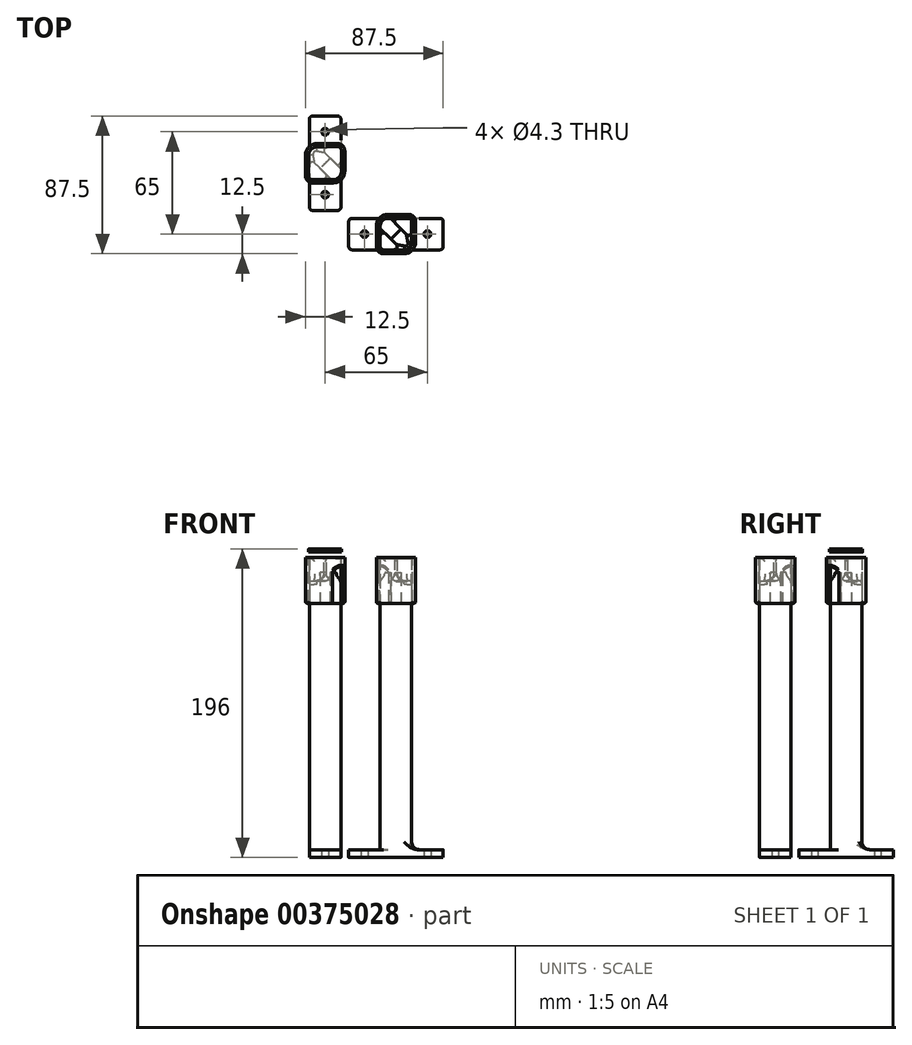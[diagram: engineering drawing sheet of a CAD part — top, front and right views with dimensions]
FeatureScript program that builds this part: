
annotation { "Feature Type Name" : "Feature", "Feature Type Description" : "" }
export const myFeature = defineFeature(function(context is Context, id is Id, definition is map)
    precondition{}
    {
        {
            var Q0;
            Q0=qCreatedBy(makeId("Top.planeOp"),FACE);
            var sketch = newSketch(context, id + "F0", { "sketchPlane" : qUnion([Q0])});
            skLineSegment(sketch, "E0.bottom", {"start": v(0, 0) * mm, "end": v(-20, 0) * mm});
            skLineSegment(sketch, "E0.top", {"start": v(0, 20) * mm, "end": v(-20, 20) * mm});
            skLineSegment(sketch, "E0.left", {"start": v(0, 0) * mm, "end": v(0, 20) * mm});
            skLineSegment(sketch, "E0.right", {"start": v(-20, 0) * mm, "end": v(-20, 20) * mm});
            skLineSegment(sketch, "E1.bottom", {"start": v(0, 40) * mm, "end": v(-20, 40) * mm});
            skLineSegment(sketch, "E1.top", {"start": v(0, -20) * mm, "end": v(-20, -20) * mm});
            skLineSegment(sketch, "E1.left", {"start": v(0, 40) * mm, "end": v(0, -20) * mm});
            skLineSegment(sketch, "E1.right", {"start": v(-20, 40) * mm, "end": v(-20, -20) * mm});
            skSolve(sketch);
        }
        {
            var Q0;
            Q0=makeQuery(id+"F0.imprint","IMPRINT",FACE,{"disambiguationData":[TD([[makeQuery(id+"F0.imprint","IMPRINT",EDGE,{"derivedFrom":sQuery(id+"F0.wireOp",EDGE,"E0.bottom")}),-1.0]])]});
            extrude(context, id + "F1", {"entities" : qUnion([Q0]), "depth" : (140 + 15 + 25 + 5) * mm});
        }
        {
            var Q0;
            {var subQ0=sQuery(id+"F0.wireOp",EDGE,"E0.top");Q0=makeQuery(id+"F0.imprint","IMPRINT",FACE,{"disambiguationData":[TD([[makeQuery(id+"F0.imprint","IMPRINT",EDGE,{"derivedFrom":subQ0}),-1.0]])]});}
            var Q1;
            {var subQ0=sQuery(id+"F0.wireOp",EDGE,"E0.bottom");Q1=makeQuery(id+"F0.imprint","IMPRINT",FACE,{"disambiguationData":[TD([[makeQuery(id+"F0.imprint","IMPRINT",EDGE,{"derivedFrom":subQ0}),1.0]])]});}
            var Q2;
            {var subQ0=sQuery(id+"F0.wireOp",EDGE,"E0.bottom");Q2=makeQuery(id+"F0.imprint","IMPRINT",FACE,{"disambiguationData":[TD([[makeQuery(id+"F0.imprint","IMPRINT",EDGE,{"derivedFrom":subQ0}),-1.0]])]});}
            extrude(context, id + "F2", {"entities" : qUnion([Q0, Q1, Q2]), "operationType" : NewBodyOperationType.ADD, "oppositeDirection" : true, "depth" : 5 * mm});
        }
        {
            var Q0;
            Q0=makeQuery(id+"F1.opExtrude","SWEPT_EDGE",EDGE,{"disambiguationData":[OSD([sQuery(id+"F0.wireOp",EDGE,"E0.bottom"),sQuery(id+"F0.wireOp",EDGE,"E1.right")])]});
            cPlane(context, id + "F3", {"entities" : qUnion([Q0]), "cplaneType" : CPlaneType.LINE_ANGLE, "offset" : 25 * mm, "angle" : 45 * degree, "width" : 150 * mm, "height" : 150 * mm});
        }
        {
            var Q0;
            Q0=qCreatedBy(id+"F3.planeOp",FACE);
            var sketch = newSketch(context, id + "F4", { "sketchPlane" : qUnion([Q0])});
            skCircle(sketch, "E2", {"center": v(0, 175) * mm, "radius": 4.5 * mm});
            skLineSegment(sketch, "E3.bottom", {"start": v(4.5, 175) * mm, "end": v(-4.5, 175) * mm});
            skLineSegment(sketch, "E3.top", {"start": v(4.5, 185) * mm, "end": v(-4.5, 185) * mm});
            skLineSegment(sketch, "E3.left", {"start": v(4.5, 175) * mm, "end": v(4.5, 185) * mm});
            skLineSegment(sketch, "E3.right", {"start": v(-4.5, 175) * mm, "end": v(-4.5, 185) * mm});
            skSolve(sketch);
        }
        {
            var Q0;
            Q0=qSketchRegion(id+"F4",true);
            extrude(context, id + "F5", {"entities" : qUnion([Q0]), "operationType" : NewBodyOperationType.REMOVE, "endBound" : BoundingType.THROUGH_ALL, "oppositeDirection" : true, "depth" : 25 * mm, "hasSecondDirection" : true, "secondDirectionBound" : SecondDirectionBoundingType.THROUGH_ALL, "secondDirectionOppositeDirection" : false, "secondDirectionDepth" : 25 * mm});
        }
        {
            var Q0;
            Q0=makeQuery(id+"F2.opExtrude","CAP_FACE",FACE,{"disambiguationData":[OSD([sQuery(id+"F0.wireOp",EDGE,"E1.bottom"),sQuery(id+"F0.wireOp",EDGE,"E1.top"),sQuery(id+"F0.wireOp",EDGE,"E1.left"),sQuery(id+"F0.wireOp",EDGE,"E1.right")])],"isStart":false});
            var sketch = newSketch(context, id + "F6", { "sketchPlane" : qUnion([Q0])});
            skCircle(sketch, "E4", {"center": v(-10, -30) * mm, "radius": 2.15 * mm});
            skPoint(sketch, "E4.centerSnap0", {"position": v(-10, -40) * mm});
            skCircle(sketch, "E5", {"center": v(-10, 10) * mm, "radius": 2.15 * mm});
            skPoint(sketch, "E5.centerSnap0", {"position": v(-10, 20) * mm});
            skSolve(sketch);
        }
        {
            var Q0;
            Q0=makeQuery(id+"F6.imprint","IMPRINT",FACE,{"disambiguationData":[TD([[makeQuery(id+"F6.imprint","IMPRINT",EDGE,{"derivedFrom":sQuery(id+"F6.wireOp",EDGE,"E4")}),1.0]])]});
            var Q1;
            Q1=makeQuery(id+"F6.imprint","IMPRINT",FACE,{"disambiguationData":[TD([[makeQuery(id+"F6.imprint","IMPRINT",EDGE,{"derivedFrom":sQuery(id+"F6.wireOp",EDGE,"E5")}),1.0]])]});
            extrude(context, id + "F7", {"entities" : qUnion([Q0, Q1]), "operationType" : NewBodyOperationType.REMOVE, "endBound" : BoundingType.THROUGH_ALL, "oppositeDirection" : true, "depth" : 25 * mm});
        }
        {
            var Q0;
            {var subQ0=sQuery(id+"F0.wireOp",EDGE,"E1.right");var subQ1=sQuery(id+"F0.wireOp",EDGE,"E0.top");Q0=makeQuery(id+"F5.boolean.opBoolean","SPLIT",EDGE,{"disambiguationData":[TD([makeQuery(id+"F2.opExtrude","CAP_FACE",FACE,{"disambiguationData":[OSD([sQuery(id+"F0.wireOp",EDGE,"E1.bottom"),sQuery(id+"F0.wireOp",EDGE,"E1.top"),sQuery(id+"F0.wireOp",EDGE,"E1.left"),subQ0])],"isStart":true})])],"derivedFrom":makeQuery(id+"F1.opExtrude","SWEPT_EDGE",EDGE,{"disambiguationData":[OSD([subQ1,subQ0])]})});}
            var Q1;
            {var subQ0=sQuery(id+"F0.wireOp",EDGE,"E1.left");var subQ1=sQuery(id+"F0.wireOp",EDGE,"E0.bottom");Q1=makeQuery(id+"F5.boolean.opBoolean","SPLIT",EDGE,{"disambiguationData":[TD([makeQuery(id+"F2.opExtrude","CAP_FACE",FACE,{"disambiguationData":[OSD([sQuery(id+"F0.wireOp",EDGE,"E1.bottom"),sQuery(id+"F0.wireOp",EDGE,"E1.top"),subQ0,sQuery(id+"F0.wireOp",EDGE,"E1.right")])],"isStart":true})])],"derivedFrom":makeQuery(id+"F1.opExtrude","SWEPT_EDGE",EDGE,{"disambiguationData":[OSD([subQ1,subQ0])]})});}
            var Q2;
            {var subQ0=sQuery(id+"F0.wireOp",EDGE,"E1.left");var subQ1=sQuery(id+"F0.wireOp",EDGE,"E0.bottom");Q2=makeQuery(id+"F5.boolean.opBoolean","SPLIT",EDGE,{"disambiguationData":[TD([makeQuery(id+"F1.opExtrude","CAP_FACE",FACE,{"disambiguationData":[OSD([subQ1,sQuery(id+"F0.wireOp",EDGE,"E0.top"),subQ0,sQuery(id+"F0.wireOp",EDGE,"E1.right")])],"isStart":false})])],"derivedFrom":makeQuery(id+"F1.opExtrude","SWEPT_EDGE",EDGE,{"disambiguationData":[OSD([subQ1,subQ0])]})});}
            var Q3;
            {var subQ0=sQuery(id+"F0.wireOp",EDGE,"E1.right");var subQ1=sQuery(id+"F0.wireOp",EDGE,"E0.top");Q3=makeQuery(id+"F5.boolean.opBoolean","SPLIT",EDGE,{"disambiguationData":[TD([makeQuery(id+"F1.opExtrude","CAP_FACE",FACE,{"disambiguationData":[OSD([sQuery(id+"F0.wireOp",EDGE,"E0.bottom"),subQ1,sQuery(id+"F0.wireOp",EDGE,"E1.left"),subQ0])],"isStart":false})])],"derivedFrom":makeQuery(id+"F1.opExtrude","SWEPT_EDGE",EDGE,{"disambiguationData":[OSD([subQ1,subQ0])]})});}
            var Q4;
            Q4=makeQuery(id+"FbTWeYtmAlg7ZSr_1.boolean.opBoolean","COPY",EDGE,{"derivedFrom":makeQuery(id+"FbTWeYtmAlg7ZSr_1.opExtrude","CAP_EDGE",EDGE,{"disambiguationData":[OSD([sQuery(id+"Fw4NKtbKTtTvk7p_1.wireOp",EDGE,"d8dff06a-fccb-4f62-b51d-daf70278856e.0")])],"isStart":true})});
            var Q5;
            Q5=makeQuery(id+"FbTWeYtmAlg7ZSr_1.boolean.opBoolean","COPY",EDGE,{"derivedFrom":makeQuery(id+"FbTWeYtmAlg7ZSr_1.opExtrude","CAP_EDGE",EDGE,{"disambiguationData":[OSD([sQuery(id+"Fw4NKtbKTtTvk7p_1.wireOp",EDGE,"ceb2908e-7de6-43f7-83ec-8949b8f8dd080.MirrorCS")])],"isStart":true})});
            var Q6;
            {var subQ0=sQuery(id+"F0.wireOp",EDGE,"E1.right");Q6=makeQuery(id+"FbTWeYtmAlg7ZSr_1.boolean.opBoolean","INTERSECT",EDGE,{"derivedFrom":[makeQuery(id+"F2.boolean.opBoolean","MERGE",FACE,{"derivedFrom":[makeQuery(id+"F1.opExtrude","SWEPT_FACE",FACE,{"disambiguationData":[OSD([subQ0])]}),makeQuery(id+"F2.opExtrude","SWEPT_FACE",FACE,{"disambiguationData":[OSD([subQ0])]})]}),makeQuery(id+"FbTWeYtmAlg7ZSr_1.opExtrude","SWEPT_FACE",FACE,{"disambiguationData":[OSD([sQuery(id+"Fw4NKtbKTtTvk7p_1.wireOp",EDGE,"ceb2908e-7de6-43f7-83ec-8949b8f8dd080.MirrorCS")])]})]});}
            var Q7;
            {var subQ0=sQuery(id+"F0.wireOp",EDGE,"E1.right");Q7=makeQuery(id+"FbTWeYtmAlg7ZSr_1.boolean.opBoolean","INTERSECT",EDGE,{"derivedFrom":[makeQuery(id+"F2.boolean.opBoolean","MERGE",FACE,{"derivedFrom":[makeQuery(id+"F1.opExtrude","SWEPT_FACE",FACE,{"disambiguationData":[OSD([subQ0])]}),makeQuery(id+"F2.opExtrude","SWEPT_FACE",FACE,{"disambiguationData":[OSD([subQ0])]})]}),makeQuery(id+"FbTWeYtmAlg7ZSr_1.opExtrude","SWEPT_FACE",FACE,{"disambiguationData":[OSD([sQuery(id+"Fw4NKtbKTtTvk7p_1.wireOp",EDGE,"d8dff06a-fccb-4f62-b51d-daf70278856e.0")])]})]});}
            fillet(context, id + "F8", {"entities" : qUnion([Q0, Q1, Q2, Q3, Q4, Q5, Q6, Q7]), "radius" : 5 * mm, "tangentPropagation" : true, "allowEdgeOverflow" : false});
        }
        {
            var Q0;
            Q0=makeQuery(id+"F2.opExtrude","SWEPT_EDGE",EDGE,{"disambiguationData":[OSD([sQuery(id+"F0.wireOp",EDGE,"E1.top"),sQuery(id+"F0.wireOp",EDGE,"E1.right")])]});
            var Q1;
            Q1=makeQuery(id+"F2.opExtrude","SWEPT_EDGE",EDGE,{"disambiguationData":[OSD([sQuery(id+"F0.wireOp",EDGE,"E1.top"),sQuery(id+"F0.wireOp",EDGE,"E1.left")])]});
            var Q2;
            Q2=makeQuery(id+"F2.opExtrude","SWEPT_EDGE",EDGE,{"disambiguationData":[OSD([sQuery(id+"F0.wireOp",EDGE,"E1.bottom"),sQuery(id+"F0.wireOp",EDGE,"E1.right")])]});
            var Q3;
            Q3=makeQuery(id+"F2.opExtrude","SWEPT_EDGE",EDGE,{"disambiguationData":[OSD([sQuery(id+"F0.wireOp",EDGE,"E1.bottom"),sQuery(id+"F0.wireOp",EDGE,"E1.left")])]});
            var Q4;
            Q4=makeQuery(id+"F1.opExtrude","SWEPT_EDGE",EDGE,{"disambiguationData":[OSD([sQuery(id+"F0.wireOp",EDGE,"E0.bottom"),sQuery(id+"F0.wireOp",EDGE,"E1.right")])]});
            var Q5;
            Q5=makeQuery(id+"F1.opExtrude","SWEPT_EDGE",EDGE,{"disambiguationData":[OSD([sQuery(id+"F0.wireOp",EDGE,"E0.top"),sQuery(id+"F0.wireOp",EDGE,"E1.left")])]});
            fillet(context, id + "F9", {"entities" : qUnion([Q0, Q1, Q2, Q3, Q4, Q5]), "radius" : 2 * mm, "tangentPropagation" : true, "allowEdgeOverflow" : false});
        }
        {
            var Q0;
            Q0=makeQuery(id+"F1.opExtrude","CAP_EDGE",EDGE,{"disambiguationData":[OSD([sQuery(id+"F0.wireOp",EDGE,"E0.bottom")])],"isStart":true});
            var Q1;
            Q1=makeQuery(id+"F1.opExtrude","CAP_EDGE",EDGE,{"disambiguationData":[OSD([sQuery(id+"F0.wireOp",EDGE,"E0.top")])],"isStart":true});
            fillet(context, id + "F10", {"entities" : qUnion([Q0, Q1]), "radius" : 5 * mm, "tangentPropagation" : true, "allowEdgeOverflow" : false});
        }
        {
            var Q0;
            Q0=makeQuery(id+"F5.boolean.opBoolean","COPY",EDGE,{"derivedFrom":makeQuery(id+"F5.opExtrude","SWEPT_EDGE",EDGE,{"disambiguationData":[OSD([sQuery(id+"F4.wireOp",EDGE,"E3.top"),sQuery(id+"F4.wireOp",EDGE,"E3.right")])]})});
            var Q1;
            Q1=makeQuery(id+"F5.boolean.opBoolean","COPY",EDGE,{"derivedFrom":makeQuery(id+"F5.opExtrude","SWEPT_EDGE",EDGE,{"disambiguationData":[OSD([sQuery(id+"F4.wireOp",EDGE,"E3.top"),sQuery(id+"F4.wireOp",EDGE,"E3.left")])]})});
            var Q2;
            Q2=makeQuery(id+"FaNR0EHfiqL3Suf_1.boolean.opBoolean","INTERSECT",EDGE,{"derivedFrom":[makeQuery(id+"F5.boolean.opBoolean","COPY",FACE,{"derivedFrom":makeQuery(id+"F5.opExtrude","SWEPT_FACE",FACE,{"disambiguationData":[OSD([sQuery(id+"F4.wireOp",EDGE,"E3.right")])]})}),makeQuery(id+"FaNR0EHfiqL3Suf_1.opExtrude","SWEPT_FACE",FACE,{"disambiguationData":[OSD([sQuery(id+"F0sESqesVKDsMNf_1.wireOp",EDGE,"yukfk0gf-0giC-ZNzu-XFQ1-qiouwhbjaQ2R")])]})]});
            var Q3;
            {var subQ0=sQuery(id+"F0.wireOp",EDGE,"E1.left");Q3=makeQuery(id+"F5.boolean.opBoolean","INTERSECT",EDGE,{"derivedFrom":[makeQuery(id+"F2.boolean.opBoolean","MERGE",FACE,{"derivedFrom":[makeQuery(id+"F1.opExtrude","SWEPT_FACE",FACE,{"disambiguationData":[OSD([subQ0])]}),makeQuery(id+"F2.opExtrude","SWEPT_FACE",FACE,{"disambiguationData":[OSD([subQ0])]})]}),makeQuery(id+"F5.opExtrude","SWEPT_FACE",FACE,{"disambiguationData":[OSD([sQuery(id+"F4.wireOp",EDGE,"E3.right")])]})]});}
            var Q4;
            {var subQ0=sQuery(id+"F0.wireOp",EDGE,"E1.right");Q4=makeQuery(id+"F5.boolean.opBoolean","INTERSECT",EDGE,{"derivedFrom":[makeQuery(id+"F2.boolean.opBoolean","MERGE",FACE,{"derivedFrom":[makeQuery(id+"F1.opExtrude","SWEPT_FACE",FACE,{"disambiguationData":[OSD([subQ0])]}),makeQuery(id+"F2.opExtrude","SWEPT_FACE",FACE,{"disambiguationData":[OSD([subQ0])]})]}),makeQuery(id+"F5.opExtrude","SWEPT_FACE",FACE,{"disambiguationData":[OSD([sQuery(id+"F4.wireOp",EDGE,"E3.left")])]})]});}
            var Q5;
            Q5=makeQuery(id+"F5.boolean.opBoolean","INTERSECT",EDGE,{"derivedFrom":[makeQuery(id+"F1.opExtrude","SWEPT_FACE",FACE,{"disambiguationData":[OSD([sQuery(id+"F0.wireOp",EDGE,"E0.top")])]}),makeQuery(id+"F5.opExtrude","SWEPT_FACE",FACE,{"disambiguationData":[OSD([sQuery(id+"F4.wireOp",EDGE,"E3.right")])]})]});
            var Q6;
            Q6=makeQuery(id+"F8.opFillet","BLEND_EDGE",EDGE,{"blendedFrom":[makeQuery(id+"F1.opExtrude","SWEPT_EDGE",EDGE,{"disambiguationData":[OSD([sQuery(id+"F0.wireOp",EDGE,"E0.top"),sQuery(id+"F0.wireOp",EDGE,"E1.right")])]}),makeQuery(id+"F5.boolean.opBoolean","COPY",FACE,{"derivedFrom":makeQuery(id+"F5.opExtrude","SWEPT_FACE",FACE,{"disambiguationData":[OSD([sQuery(id+"F4.wireOp",EDGE,"E2")])]})})],"blendedInto":[makeQuery(id+"F5.boolean.opBoolean","COPY",FACE,{"derivedFrom":makeQuery(id+"F5.opExtrude","SWEPT_FACE",FACE,{"disambiguationData":[OSD([sQuery(id+"F4.wireOp",EDGE,"E2")])]})})]});
            var Q7;
            Q7=makeQuery(id+"F5.boolean.opBoolean","INTERSECT",EDGE,{"derivedFrom":[makeQuery(id+"F1.opExtrude","SWEPT_FACE",FACE,{"disambiguationData":[OSD([sQuery(id+"F0.wireOp",EDGE,"E0.top")])]}),makeQuery(id+"F5.opExtrude","SWEPT_FACE",FACE,{"disambiguationData":[OSD([sQuery(id+"F4.wireOp",EDGE,"E2")])]})]});
            var Q8;
            {var subQ0=sQuery(id+"F0.wireOp",EDGE,"E1.right");Q8=makeQuery(id+"F5.boolean.opBoolean","INTERSECT",EDGE,{"derivedFrom":[makeQuery(id+"F2.boolean.opBoolean","MERGE",FACE,{"derivedFrom":[makeQuery(id+"F1.opExtrude","SWEPT_FACE",FACE,{"disambiguationData":[OSD([subQ0])]}),makeQuery(id+"F2.opExtrude","SWEPT_FACE",FACE,{"disambiguationData":[OSD([subQ0])]})]}),makeQuery(id+"F5.opExtrude","SWEPT_FACE",FACE,{"disambiguationData":[OSD([sQuery(id+"F4.wireOp",EDGE,"E2")])]})]});}
            var Q9;
            Q9=makeQuery(id+"F5.boolean.opBoolean","INTERSECT",EDGE,{"derivedFrom":[makeQuery(id+"F1.opExtrude","SWEPT_FACE",FACE,{"disambiguationData":[OSD([sQuery(id+"F0.wireOp",EDGE,"E0.bottom")])]}),makeQuery(id+"F5.opExtrude","SWEPT_FACE",FACE,{"disambiguationData":[OSD([sQuery(id+"F4.wireOp",EDGE,"E3.left")])]})]});
            var Q10;
            Q10=makeQuery(id+"F5.boolean.opBoolean","INTERSECT",EDGE,{"derivedFrom":[makeQuery(id+"F1.opExtrude","SWEPT_FACE",FACE,{"disambiguationData":[OSD([sQuery(id+"F0.wireOp",EDGE,"E0.bottom")])]}),makeQuery(id+"F5.opExtrude","SWEPT_FACE",FACE,{"disambiguationData":[OSD([sQuery(id+"F4.wireOp",EDGE,"E2")])]})]});
            var Q11;
            Q11=makeQuery(id+"F8.opFillet","BLEND_EDGE",EDGE,{"blendedFrom":[makeQuery(id+"F1.opExtrude","SWEPT_EDGE",EDGE,{"disambiguationData":[OSD([sQuery(id+"F0.wireOp",EDGE,"E0.bottom"),sQuery(id+"F0.wireOp",EDGE,"E1.left")])]}),makeQuery(id+"F5.boolean.opBoolean","COPY",FACE,{"derivedFrom":makeQuery(id+"F5.opExtrude","SWEPT_FACE",FACE,{"disambiguationData":[OSD([sQuery(id+"F4.wireOp",EDGE,"E2")])]})})],"blendedInto":[makeQuery(id+"F5.boolean.opBoolean","COPY",FACE,{"derivedFrom":makeQuery(id+"F5.opExtrude","SWEPT_FACE",FACE,{"disambiguationData":[OSD([sQuery(id+"F4.wireOp",EDGE,"E2")])]})})]});
            var Q12;
            {var subQ0=sQuery(id+"F0.wireOp",EDGE,"E1.left");Q12=makeQuery(id+"F5.boolean.opBoolean","INTERSECT",EDGE,{"derivedFrom":[makeQuery(id+"F2.boolean.opBoolean","MERGE",FACE,{"derivedFrom":[makeQuery(id+"F1.opExtrude","SWEPT_FACE",FACE,{"disambiguationData":[OSD([subQ0])]}),makeQuery(id+"F2.opExtrude","SWEPT_FACE",FACE,{"disambiguationData":[OSD([subQ0])]})]}),makeQuery(id+"F5.opExtrude","SWEPT_FACE",FACE,{"disambiguationData":[OSD([sQuery(id+"F4.wireOp",EDGE,"E2")])]})]});}
            fillet(context, id + "F11", {"entities" : qUnion([Q0, Q1, Q2, Q3, Q4, Q5, Q6, Q7, Q8, Q9, Q10, Q11, Q12]), "radius" : 2 * mm, "tangentPropagation" : true, "allowEdgeOverflow" : false});
        }
        {
            var Q0;
            {var subQ0=sQuery(id+"F0.wireOp",EDGE,"E0.top");var subQ1=sQuery(id+"F0.wireOp",EDGE,"E1.left");Q0=makeQuery(id+"F5.boolean.opBoolean","SPLIT",FACE,{"disambiguationData":[TD([makeQuery(id+"F1.opExtrude","SWEPT_FACE",FACE,{"disambiguationData":[OSD([subQ0])]})])],"derivedFrom":makeQuery(id+"F1.opExtrude","CAP_FACE",FACE,{"disambiguationData":[OSD([sQuery(id+"F0.wireOp",EDGE,"E0.bottom"),subQ0,subQ1,sQuery(id+"F0.wireOp",EDGE,"E1.right")])],"isStart":false})});}
            var sketch = newSketch(context, id + "F12", { "sketchPlane" : qUnion([Q0])});
            skLineSegment(sketch, "E6.0", {"start": v(2.5, 18) * mm, "end": v(2.5, 11.2) * mm});
            skLineSegment(sketch, "E6.1", {"start": v(-22.5, 8.8) * mm, "end": v(-22.5, 15) * mm});
            skArc(sketch, "E6.2", {"start": v(-22.5, 15) * mm, "mid": v(-20.3, 20.3) * mm, "end": v(-15, 22.5) * mm});
            skLineSegment(sketch, "E6.3", {"start": v(-15, 22.5) * mm, "end": v(-8.8, 22.5) * mm});
            skLineSegment(sketch, "E6.4", {"start": v(-2, 22.5) * mm, "end": v(-8.8, 22.5) * mm});
            skLineSegment(sketch, "E6.5", {"start": v(-22.5, 8.8) * mm, "end": v(-22.5, 2) * mm});
            skArc(sketch, "E6.6", {"start": v(2.5, 18) * mm, "mid": v(1.18, 21.18) * mm, "end": v(-2, 22.5) * mm});
            skArc(sketch, "E6.7", {"start": v(-22.5, 2) * mm, "mid": v(-21.18, -1.18) * mm, "end": v(-18, -2.5) * mm});
            skLineSegment(sketch, "E6.8", {"start": v(-11.2, -2.5) * mm, "end": v(-18, -2.5) * mm});
            skLineSegment(sketch, "E6.9", {"start": v(-5, -2.5) * mm, "end": v(-11.2, -2.5) * mm});
            skArc(sketch, "E6.10", {"start": v(2.5, 5) * mm, "mid": v(0.3, -0.3) * mm, "end": v(-5, -2.5) * mm});
            skLineSegment(sketch, "E6.11", {"start": v(2.5, 11.2) * mm, "end": v(2.5, 5) * mm});
            skArc(sketch, "E7.0", {"start": v(0.5, 18) * mm, "mid": v(-0.23, 19.77) * mm, "end": v(-2, 20.5) * mm});
            skLineSegment(sketch, "E7.1", {"start": v(-20.5, 8.8) * mm, "end": v(-20.5, 2) * mm});
            skLineSegment(sketch, "E7.2", {"start": v(-20.5, 8.8) * mm, "end": v(-20.5, 15) * mm});
            skArc(sketch, "E7.3", {"start": v(-20.5, 15) * mm, "mid": v(-18.89, 18.89) * mm, "end": v(-15, 20.5) * mm});
            skLineSegment(sketch, "E7.4", {"start": v(-15, 20.5) * mm, "end": v(-8.8, 20.5) * mm});
            skArc(sketch, "E7.5", {"start": v(-20.5, 2) * mm, "mid": v(-19.77, 0.23) * mm, "end": v(-18, -0.5) * mm});
            skLineSegment(sketch, "E7.6", {"start": v(-2, 20.5) * mm, "end": v(-8.8, 20.5) * mm});
            skLineSegment(sketch, "E7.7", {"start": v(-11.2, -0.5) * mm, "end": v(-18, -0.5) * mm});
            skLineSegment(sketch, "E7.8", {"start": v(-5, -0.5) * mm, "end": v(-11.2, -0.5) * mm});
            skArc(sketch, "E7.9", {"start": v(0.5, 5) * mm, "mid": v(-1.11, 1.11) * mm, "end": v(-5, -0.5) * mm});
            skLineSegment(sketch, "E7.10", {"start": v(0.5, 11.2) * mm, "end": v(0.5, 5) * mm});
            skLineSegment(sketch, "E7.11", {"start": v(0.5, 18) * mm, "end": v(0.5, 11.2) * mm});
            skSolve(sketch);
        }
        {
            var Q0;
            Q0=makeQuery(id+"F12.imprint","IMPRINT",FACE,{"disambiguationData":[TD([[makeQuery(id+"F12.imprint","IMPRINT",EDGE,{"derivedFrom":sQuery(id+"F12.wireOp",EDGE,"E6.0")}),-1.0]])]});
            extrude(context, id + "F13", {"entities" : qUnion([Q0]), "oppositeDirection" : true, "depth" : 25 * mm, "hasSecondDirection" : true, "secondDirectionOppositeDirection" : false, "secondDirectionDepth" : 4 * mm});
        }
        {
            var Q0;
            Q0=makeQuery(id+"F13.opExtrude","CAP_FACE",FACE,{"disambiguationData":[OSD([sQuery(id+"F12.wireOp",EDGE,"E6.0"),sQuery(id+"F12.wireOp",EDGE,"E6.1"),sQuery(id+"F12.wireOp",EDGE,"E6.2"),sQuery(id+"F12.wireOp",EDGE,"E6.3"),sQuery(id+"F12.wireOp",EDGE,"E6.4"),sQuery(id+"F12.wireOp",EDGE,"E6.5"),sQuery(id+"F12.wireOp",EDGE,"E6.6"),sQuery(id+"F12.wireOp",EDGE,"E6.7"),sQuery(id+"F12.wireOp",EDGE,"E6.8"),sQuery(id+"F12.wireOp",EDGE,"E6.9"),sQuery(id+"F12.wireOp",EDGE,"E6.10"),sQuery(id+"F12.wireOp",EDGE,"E6.11"),sQuery(id+"F12.wireOp",EDGE,"E7.0"),sQuery(id+"F12.wireOp",EDGE,"E7.1"),sQuery(id+"F12.wireOp",EDGE,"E7.2"),sQuery(id+"F12.wireOp",EDGE,"E7.3"),sQuery(id+"F12.wireOp",EDGE,"E7.4"),sQuery(id+"F12.wireOp",EDGE,"E7.5"),sQuery(id+"F12.wireOp",EDGE,"E7.6"),sQuery(id+"F12.wireOp",EDGE,"E7.7"),sQuery(id+"F12.wireOp",EDGE,"E7.8"),sQuery(id+"F12.wireOp",EDGE,"E7.9"),sQuery(id+"F12.wireOp",EDGE,"E7.10"),sQuery(id+"F12.wireOp",EDGE,"E7.11")])],"isStart":true});
            var sketch = newSketch(context, id + "F14", { "sketchPlane" : qUnion([Q0])});
            skLineSegment(sketch, "E8.0.0", {"start": v(-22.5, 15) * mm, "end": v(-22.5, 2) * mm});
            skArc(sketch, "E8.0.1", {"start": v(-22.5, 2) * mm, "mid": v(-21.18, -1.18) * mm, "end": v(-18, -2.5) * mm});
            skLineSegment(sketch, "E8.0.2", {"start": v(-18, -2.5) * mm, "end": v(-5, -2.5) * mm});
            skArc(sketch, "E8.0.3", {"start": v(-5, -2.5) * mm, "mid": v(0.3, -0.3) * mm, "end": v(2.5, 5) * mm});
            skLineSegment(sketch, "E8.0.4", {"start": v(2.5, 5) * mm, "end": v(2.5, 18) * mm});
            skArc(sketch, "E8.0.5", {"start": v(2.5, 18) * mm, "mid": v(1.18, 21.18) * mm, "end": v(-2, 22.5) * mm});
            skLineSegment(sketch, "E8.0.6", {"start": v(-2, 22.5) * mm, "end": v(-15, 22.5) * mm});
            skArc(sketch, "E8.0.7", {"start": v(-15, 22.5) * mm, "mid": v(-20.3, 20.3) * mm, "end": v(-22.5, 15) * mm});
            skSolve(sketch);
        }
        {
            var Q0;
            Q0=makeQuery(id+"F14.imprint","IMPRINT",FACE,{"disambiguationData":[TD([[makeQuery(id+"F14.imprint","IMPRINT",EDGE,{"derivedFrom":sQuery(id+"F14.wireOp",EDGE,"E8.0.0")}),1.0]])]});
            var Q1;
            Q1=makeQuery(id+"F14.imprint","IMPRINT",FACE,{"disambiguationData":[TD([[makeQuery(id+"F14.imprint","IMPRINT",EDGE,{"derivedFrom":makeQuery(id+"F13.opExtrude","CAP_EDGE",EDGE,{"disambiguationData":[OSD([sQuery(id+"F12.wireOp",EDGE,"E7.0")])],"isStart":true})}),1.0]])]});
            extrude(context, id + "F15", {"entities" : qUnion([Q0, Q1]), "operationType" : NewBodyOperationType.ADD, "depth" : 2 * mm});
        }
        {
            var Q0;
            Q0=makeQuery(id+"F13.opExtrude","SWEPT_BODY",BODY,{"disambiguationData":[OSD([sQuery(id+"F12.wireOp",EDGE,"E6.0"),sQuery(id+"F12.wireOp",EDGE,"E6.1"),sQuery(id+"F12.wireOp",EDGE,"E6.2"),sQuery(id+"F12.wireOp",EDGE,"E6.3"),sQuery(id+"F12.wireOp",EDGE,"E6.4"),sQuery(id+"F12.wireOp",EDGE,"E6.5"),sQuery(id+"F12.wireOp",EDGE,"E6.6"),sQuery(id+"F12.wireOp",EDGE,"E6.7"),sQuery(id+"F12.wireOp",EDGE,"E6.8"),sQuery(id+"F12.wireOp",EDGE,"E6.9"),sQuery(id+"F12.wireOp",EDGE,"E6.10"),sQuery(id+"F12.wireOp",EDGE,"E6.11"),sQuery(id+"F12.wireOp",EDGE,"E7.0"),sQuery(id+"F12.wireOp",EDGE,"E7.1"),sQuery(id+"F12.wireOp",EDGE,"E7.2"),sQuery(id+"F12.wireOp",EDGE,"E7.3"),sQuery(id+"F12.wireOp",EDGE,"E7.4"),sQuery(id+"F12.wireOp",EDGE,"E7.5"),sQuery(id+"F12.wireOp",EDGE,"E7.6"),sQuery(id+"F12.wireOp",EDGE,"E7.7"),sQuery(id+"F12.wireOp",EDGE,"E7.8"),sQuery(id+"F12.wireOp",EDGE,"E7.9"),sQuery(id+"F12.wireOp",EDGE,"E7.10"),sQuery(id+"F12.wireOp",EDGE,"E7.11")])]});
            transform(context, id + "F16", {"entities" : qUnion([Q0]), "transformType" : TransformType.TRANSLATION_3D, "dx" : 0 * mm, "dy" : 0 * mm, "dz" : -3.5 * mm, "makeCopy" : false});
        }
        {
            var Q0;
            Q0=qCreatedBy(id+"F3.planeOp",FACE);
            cPlane(context, id + "F17", {"entities" : qUnion([Q0]), "cplaneType" : CPlaneType.OFFSET, "offset" : 0 * mm, "width" : 150 * mm, "height" : 150 * mm});
        }
        {
            var Q0;
            Q0=qCreatedBy(id+"F17.planeOp",FACE);
            var sketch = newSketch(context, id + "F18", { "sketchPlane" : qUnion([Q0])});
            skArc(sketch, "E9", {"start": v(4.63, 175) * mm, "mid": v(0, 179.62) * mm, "end": v(-4.62, 175) * mm});
            skLineSegment(sketch, "E10", {"start": v(4.63, 175) * mm, "end": v(4.63, 156.5) * mm});
            skLineSegment(sketch, "E11", {"start": v(-4.62, 175) * mm, "end": v(-4.62, 156.5) * mm});
            skLineSegment(sketch, "E12", {"start": v(-4.63, 156.5) * mm, "end": v(4.63, 156.5) * mm});
            skSolve(sketch);
        }
        {
            var Q0;
            Q0=qSketchRegion(id+"F18",true);
            extrude(context, id + "F19", {"entities" : qUnion([Q0]), "operationType" : NewBodyOperationType.REMOVE, "endBound" : BoundingType.THROUGH_ALL, "oppositeDirection" : true, "depth" : 25 * mm});
        }
        {
            var Q0;
            Q0=makeQuery(id+"F19.boolean.opBoolean","COPY",FACE,{"derivedFrom":makeQuery(id+"F19.opExtrude","SWEPT_FACE",FACE,{"disambiguationData":[OSD([sQuery(id+"F18.wireOp",EDGE,"E10")])]})});
            var Q1;
            Q1=makeQuery(id+"F19.boolean.opBoolean","COPY",FACE,{"derivedFrom":makeQuery(id+"F19.opExtrude","SWEPT_FACE",FACE,{"disambiguationData":[OSD([sQuery(id+"F18.wireOp",EDGE,"E9")])]})});
            var Q2;
            Q2=makeQuery(id+"F19.boolean.opBoolean","COPY",FACE,{"derivedFrom":makeQuery(id+"F19.opExtrude","SWEPT_FACE",FACE,{"disambiguationData":[OSD([sQuery(id+"F18.wireOp",EDGE,"E11")])]})});
            fillet(context, id + "F20", {"entities" : qUnion([Q0, Q1, Q2]), "radius" : 1 * mm, "tangentPropagation" : true, "allowEdgeOverflow" : false});
        }
        {
            var Q0;
            Q0=makeQuery(id+"F13.opExtrude","CAP_FACE",FACE,{"disambiguationData":[OSD([sQuery(id+"F12.wireOp",EDGE,"E6.0"),sQuery(id+"F12.wireOp",EDGE,"E6.1"),sQuery(id+"F12.wireOp",EDGE,"E6.2"),sQuery(id+"F12.wireOp",EDGE,"E6.3"),sQuery(id+"F12.wireOp",EDGE,"E6.4"),sQuery(id+"F12.wireOp",EDGE,"E6.5"),sQuery(id+"F12.wireOp",EDGE,"E6.6"),sQuery(id+"F12.wireOp",EDGE,"E6.7"),sQuery(id+"F12.wireOp",EDGE,"E6.8"),sQuery(id+"F12.wireOp",EDGE,"E6.9"),sQuery(id+"F12.wireOp",EDGE,"E6.10"),sQuery(id+"F12.wireOp",EDGE,"E6.11"),sQuery(id+"F12.wireOp",EDGE,"E7.0"),sQuery(id+"F12.wireOp",EDGE,"E7.1"),sQuery(id+"F12.wireOp",EDGE,"E7.2"),sQuery(id+"F12.wireOp",EDGE,"E7.3"),sQuery(id+"F12.wireOp",EDGE,"E7.4"),sQuery(id+"F12.wireOp",EDGE,"E7.5"),sQuery(id+"F12.wireOp",EDGE,"E7.6"),sQuery(id+"F12.wireOp",EDGE,"E7.7"),sQuery(id+"F12.wireOp",EDGE,"E7.8"),sQuery(id+"F12.wireOp",EDGE,"E7.9"),sQuery(id+"F12.wireOp",EDGE,"E7.10"),sQuery(id+"F12.wireOp",EDGE,"E7.11")])],"isStart":false});
            fillet(context, id + "F21", {"entities" : qUnion([Q0]), "radius" : 1 * mm, "tangentPropagation" : true, "allowEdgeOverflow" : false});
        }
        {
            var Q0;
            Q0=makeQuery(id+"F1.opExtrude","SWEPT_BODY",BODY,{"disambiguationData":[OSD([sQuery(id+"F0.wireOp",EDGE,"E0.bottom"),sQuery(id+"F0.wireOp",EDGE,"E0.top"),sQuery(id+"F0.wireOp",EDGE,"E1.left"),sQuery(id+"F0.wireOp",EDGE,"E1.right")])]});
            var Q1;
            Q1=makeQuery(id+"F13.opExtrude","SWEPT_BODY",BODY,{"disambiguationData":[OSD([sQuery(id+"F12.wireOp",EDGE,"E6.0"),sQuery(id+"F12.wireOp",EDGE,"E6.1"),sQuery(id+"F12.wireOp",EDGE,"E6.2"),sQuery(id+"F12.wireOp",EDGE,"E6.3"),sQuery(id+"F12.wireOp",EDGE,"E6.4"),sQuery(id+"F12.wireOp",EDGE,"E6.5"),sQuery(id+"F12.wireOp",EDGE,"E6.6"),sQuery(id+"F12.wireOp",EDGE,"E6.7"),sQuery(id+"F12.wireOp",EDGE,"E6.8"),sQuery(id+"F12.wireOp",EDGE,"E6.9"),sQuery(id+"F12.wireOp",EDGE,"E6.10"),sQuery(id+"F12.wireOp",EDGE,"E6.11"),sQuery(id+"F12.wireOp",EDGE,"E7.0"),sQuery(id+"F12.wireOp",EDGE,"E7.1"),sQuery(id+"F12.wireOp",EDGE,"E7.2"),sQuery(id+"F12.wireOp",EDGE,"E7.3"),sQuery(id+"F12.wireOp",EDGE,"E7.4"),sQuery(id+"F12.wireOp",EDGE,"E7.5"),sQuery(id+"F12.wireOp",EDGE,"E7.6"),sQuery(id+"F12.wireOp",EDGE,"E7.7"),sQuery(id+"F12.wireOp",EDGE,"E7.8"),sQuery(id+"F12.wireOp",EDGE,"E7.9"),sQuery(id+"F12.wireOp",EDGE,"E7.10"),sQuery(id+"F12.wireOp",EDGE,"E7.11")])]});
            var Q2;
            Q2=qCreatedBy(makeId("Right.planeOp"),FACE);
            mirror(context, id + "F22", {"entities" : qUnion([Q0, Q1]), "mirrorPlane" : qUnion([Q2])});
        }
        {
            var Q0;
            Q0=makeQuery(id+"F22.opPattern","COPY",BODY,{"derivedFrom":makeQuery(id+"F1.opExtrude","SWEPT_BODY",BODY,{"disambiguationData":[OSD([sQuery(id+"F0.wireOp",EDGE,"E0.bottom"),sQuery(id+"F0.wireOp",EDGE,"E0.top"),sQuery(id+"F0.wireOp",EDGE,"E1.left"),sQuery(id+"F0.wireOp",EDGE,"E1.right")])]}),"instanceName":"1"});
            var Q1;
            Q1=makeQuery(id+"F22.opPattern","COPY",BODY,{"derivedFrom":makeQuery(id+"F13.opExtrude","SWEPT_BODY",BODY,{"disambiguationData":[OSD([sQuery(id+"F12.wireOp",EDGE,"E6.0"),sQuery(id+"F12.wireOp",EDGE,"E6.1"),sQuery(id+"F12.wireOp",EDGE,"E6.2"),sQuery(id+"F12.wireOp",EDGE,"E6.3"),sQuery(id+"F12.wireOp",EDGE,"E6.4"),sQuery(id+"F12.wireOp",EDGE,"E6.5"),sQuery(id+"F12.wireOp",EDGE,"E6.6"),sQuery(id+"F12.wireOp",EDGE,"E6.7"),sQuery(id+"F12.wireOp",EDGE,"E6.8"),sQuery(id+"F12.wireOp",EDGE,"E6.9"),sQuery(id+"F12.wireOp",EDGE,"E6.10"),sQuery(id+"F12.wireOp",EDGE,"E6.11"),sQuery(id+"F12.wireOp",EDGE,"E7.0"),sQuery(id+"F12.wireOp",EDGE,"E7.1"),sQuery(id+"F12.wireOp",EDGE,"E7.2"),sQuery(id+"F12.wireOp",EDGE,"E7.3"),sQuery(id+"F12.wireOp",EDGE,"E7.4"),sQuery(id+"F12.wireOp",EDGE,"E7.5"),sQuery(id+"F12.wireOp",EDGE,"E7.6"),sQuery(id+"F12.wireOp",EDGE,"E7.7"),sQuery(id+"F12.wireOp",EDGE,"E7.8"),sQuery(id+"F12.wireOp",EDGE,"E7.9"),sQuery(id+"F12.wireOp",EDGE,"E7.10"),sQuery(id+"F12.wireOp",EDGE,"E7.11")])]}),"instanceName":"1"});
            transform(context, id + "F23", {"entities" : qUnion([Q0, Q1]), "transformType" : TransformType.TRANSLATION_3D, "dx" : 30 * mm, "dy" : 0 * mm, "dz" : 0 * mm, "makeCopy" : false});
        }
        {
            var Q0;
            Q0=makeQuery(id+"F22.opPattern","COPY",BODY,{"derivedFrom":makeQuery(id+"F1.opExtrude","SWEPT_BODY",BODY,{"disambiguationData":[OSD([sQuery(id+"F0.wireOp",EDGE,"E0.bottom"),sQuery(id+"F0.wireOp",EDGE,"E0.top"),sQuery(id+"F0.wireOp",EDGE,"E1.left"),sQuery(id+"F0.wireOp",EDGE,"E1.right")])]}),"instanceName":"1"});
            var Q1;
            Q1=makeQuery(id+"F22.opPattern","COPY",BODY,{"derivedFrom":makeQuery(id+"F13.opExtrude","SWEPT_BODY",BODY,{"disambiguationData":[OSD([sQuery(id+"F12.wireOp",EDGE,"E6.0"),sQuery(id+"F12.wireOp",EDGE,"E6.1"),sQuery(id+"F12.wireOp",EDGE,"E6.2"),sQuery(id+"F12.wireOp",EDGE,"E6.3"),sQuery(id+"F12.wireOp",EDGE,"E6.4"),sQuery(id+"F12.wireOp",EDGE,"E6.5"),sQuery(id+"F12.wireOp",EDGE,"E6.6"),sQuery(id+"F12.wireOp",EDGE,"E6.7"),sQuery(id+"F12.wireOp",EDGE,"E6.8"),sQuery(id+"F12.wireOp",EDGE,"E6.9"),sQuery(id+"F12.wireOp",EDGE,"E6.10"),sQuery(id+"F12.wireOp",EDGE,"E6.11"),sQuery(id+"F12.wireOp",EDGE,"E7.0"),sQuery(id+"F12.wireOp",EDGE,"E7.1"),sQuery(id+"F12.wireOp",EDGE,"E7.2"),sQuery(id+"F12.wireOp",EDGE,"E7.3"),sQuery(id+"F12.wireOp",EDGE,"E7.4"),sQuery(id+"F12.wireOp",EDGE,"E7.5"),sQuery(id+"F12.wireOp",EDGE,"E7.6"),sQuery(id+"F12.wireOp",EDGE,"E7.7"),sQuery(id+"F12.wireOp",EDGE,"E7.8"),sQuery(id+"F12.wireOp",EDGE,"E7.9"),sQuery(id+"F12.wireOp",EDGE,"E7.10"),sQuery(id+"F12.wireOp",EDGE,"E7.11")])]}),"instanceName":"1"});
            var Q2;
            {var subQ0=sQuery(id+"F0.wireOp",EDGE,"E1.left");Q2=makeQuery(id+"F8.opFillet","BLEND_EDGE",EDGE,{"blendedFrom":[makeQuery(id+"F1.opExtrude","SWEPT_EDGE",EDGE,{"disambiguationData":[OSD([sQuery(id+"F0.wireOp",EDGE,"E0.bottom"),subQ0])]}),makeQuery(id+"F2.boolean.opBoolean","MERGE",FACE,{"derivedFrom":[makeQuery(id+"F1.opExtrude","SWEPT_FACE",FACE,{"disambiguationData":[OSD([subQ0])]}),makeQuery(id+"F2.opExtrude","SWEPT_FACE",FACE,{"disambiguationData":[OSD([subQ0])]})]})],"blendedInto":[makeQuery(id+"F2.boolean.opBoolean","MERGE",FACE,{"derivedFrom":[makeQuery(id+"F1.opExtrude","SWEPT_FACE",FACE,{"disambiguationData":[OSD([subQ0])]}),makeQuery(id+"F2.opExtrude","SWEPT_FACE",FACE,{"disambiguationData":[OSD([subQ0])]})]})]});}
            transform(context, id + "F24", {"entities" : qUnion([Q0, Q1]), "transformType" : TransformType.ROTATION, "transformAxis" : qUnion([Q2]), "angle" : 90 * degree, "makeCopy" : false});
        }
        {
            var Q0;
            Q0=makeQuery(id+"F22.opPattern","COPY",BODY,{"derivedFrom":makeQuery(id+"F1.opExtrude","SWEPT_BODY",BODY,{"disambiguationData":[OSD([sQuery(id+"F0.wireOp",EDGE,"E0.bottom"),sQuery(id+"F0.wireOp",EDGE,"E0.top"),sQuery(id+"F0.wireOp",EDGE,"E1.left"),sQuery(id+"F0.wireOp",EDGE,"E1.right")])]}),"instanceName":"1"});
            var Q1;
            Q1=makeQuery(id+"F22.opPattern","COPY",BODY,{"derivedFrom":makeQuery(id+"F13.opExtrude","SWEPT_BODY",BODY,{"disambiguationData":[OSD([sQuery(id+"F12.wireOp",EDGE,"E6.0"),sQuery(id+"F12.wireOp",EDGE,"E6.1"),sQuery(id+"F12.wireOp",EDGE,"E6.2"),sQuery(id+"F12.wireOp",EDGE,"E6.3"),sQuery(id+"F12.wireOp",EDGE,"E6.4"),sQuery(id+"F12.wireOp",EDGE,"E6.5"),sQuery(id+"F12.wireOp",EDGE,"E6.6"),sQuery(id+"F12.wireOp",EDGE,"E6.7"),sQuery(id+"F12.wireOp",EDGE,"E6.8"),sQuery(id+"F12.wireOp",EDGE,"E6.9"),sQuery(id+"F12.wireOp",EDGE,"E6.10"),sQuery(id+"F12.wireOp",EDGE,"E6.11"),sQuery(id+"F12.wireOp",EDGE,"E7.0"),sQuery(id+"F12.wireOp",EDGE,"E7.1"),sQuery(id+"F12.wireOp",EDGE,"E7.2"),sQuery(id+"F12.wireOp",EDGE,"E7.3"),sQuery(id+"F12.wireOp",EDGE,"E7.4"),sQuery(id+"F12.wireOp",EDGE,"E7.5"),sQuery(id+"F12.wireOp",EDGE,"E7.6"),sQuery(id+"F12.wireOp",EDGE,"E7.7"),sQuery(id+"F12.wireOp",EDGE,"E7.8"),sQuery(id+"F12.wireOp",EDGE,"E7.9"),sQuery(id+"F12.wireOp",EDGE,"E7.10"),sQuery(id+"F12.wireOp",EDGE,"E7.11")])]}),"instanceName":"1"});
            transform(context, id + "F25", {"entities" : qUnion([Q0, Q1]), "transformType" : TransformType.TRANSLATION_3D, "dx" : 30 * mm, "dy" : 0 * mm, "dz" : 0 * mm, "makeCopy" : false});
        }
    });
